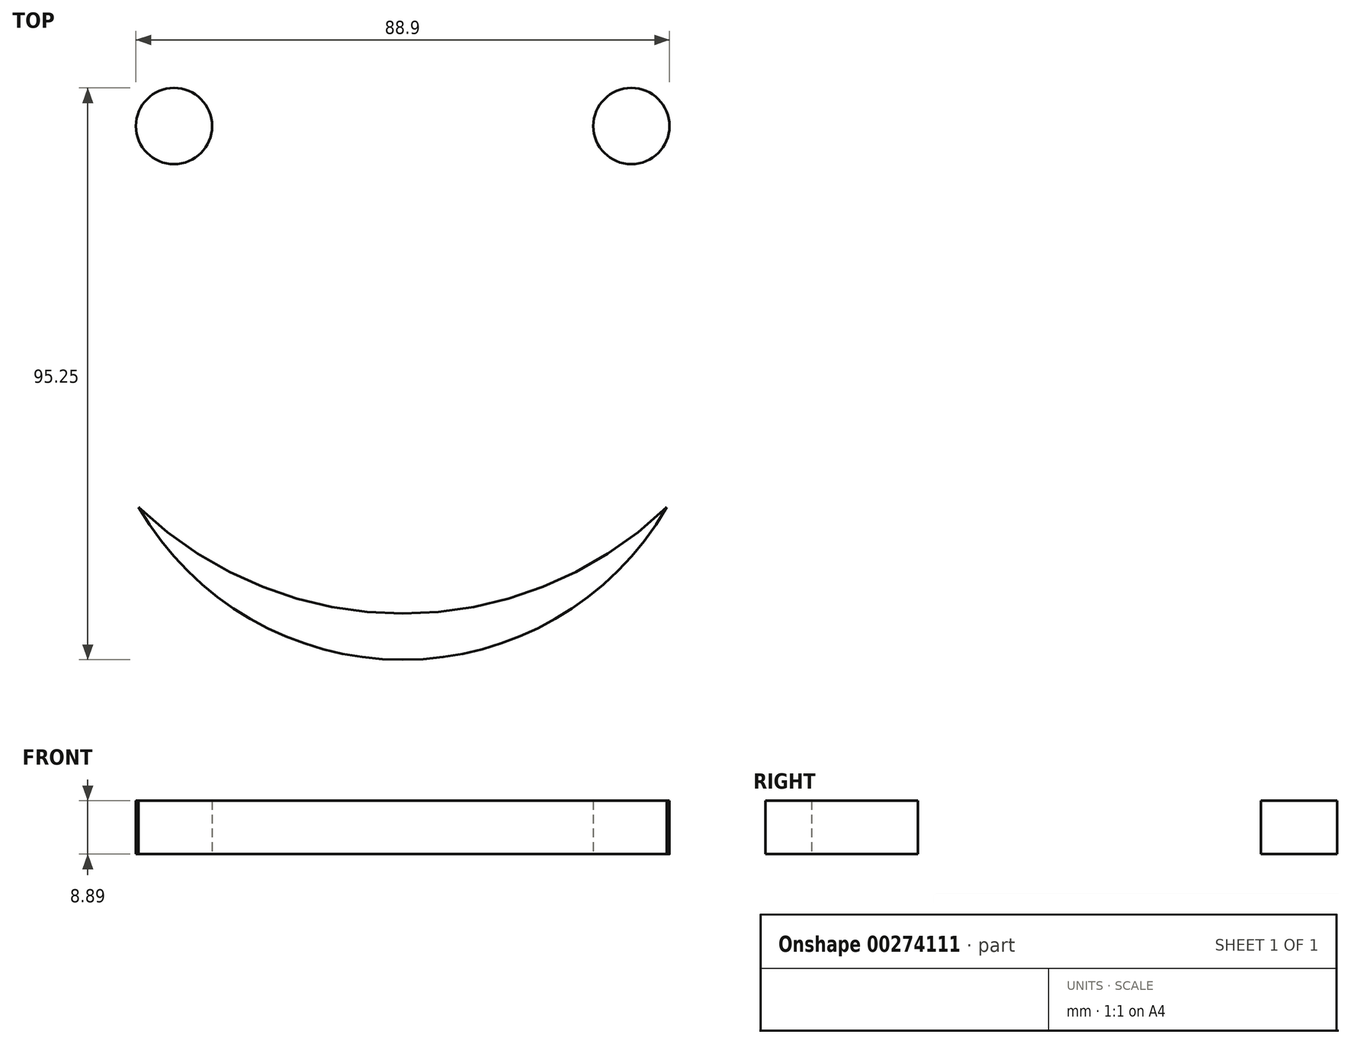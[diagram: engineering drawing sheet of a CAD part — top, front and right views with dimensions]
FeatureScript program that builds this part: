
annotation { "Feature Type Name" : "Feature", "Feature Type Description" : "" }
export const myFeature = defineFeature(function(context is Context, id is Id, definition is map)
    precondition{}
    {
        {
            var Q0;
            Q0=qCreatedBy(makeId("Top.planeOp"),FACE);
            var sketch = newSketch(context, id + "F0", { "sketchPlane" : qUnion([Q0])});
            skCircle(sketch, "E0", {"center": v(-38.1, 38.1) * mm, "radius": 6.35 * mm});
            skCircle(sketch, "E1", {"center": v(38.1, 38.1) * mm, "radius": 6.35 * mm});
            skArc(sketch, "E2", {"start": v(-44, -25.4) * mm, "mid": v(0, -50.8) * mm, "end": v(44, -25.4) * mm});
            skPoint(sketch, "E3", {"position": v(-44, -25.4) * mm});
            skArc(sketch, "E4", {"start": v(44, -25.4) * mm, "mid": v(0, -43.1) * mm, "end": v(-44, -25.4) * mm});
            skSolve(sketch);
        }
        {
            var Q0;
            Q0 = qSketchRegion(id + "F0", true);
            extrude(context, id + "F1", {"entities" : qUnion([Q0]), "depth" : 8.9 * mm});
        }
    });
